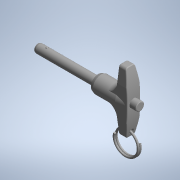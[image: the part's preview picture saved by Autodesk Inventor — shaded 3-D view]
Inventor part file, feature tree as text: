
AUTODESK INVENTOR PART (.ipt)
format: ipt  version: 2022.3 (Build 263350000, 350)  size: 407,040 bytes
history: native  units: mm (DEFAULTED — no unit token found)
features: mirror x2, revolve x1, fillet x1, sweep x1
ambient origin geometry x8: Origin, YZ Plane, XZ Plane, XY Plane, X Axis, Y Axis, Z Axis, Center Point
bodies: Solid1 (feature_tree), Solid2 (feature_tree), Solid3 (feature_tree), Solid4 (feature_tree), Solid5 (feature_tree)
feature tree (5):
  revolve  "Revolve2"  [1 undecoded]
  mirror  "Mirror2"
  mirror  "Mirror1[1]"
  fillet  "Fillet4"  [1 undecoded]
  sweep  "Sweep2"
note: 2 required parameter values undecoded (feature->parameter linkage not recoverable at this tier; creation-order binding heuristic only, values carry confidence <= 0.55)
